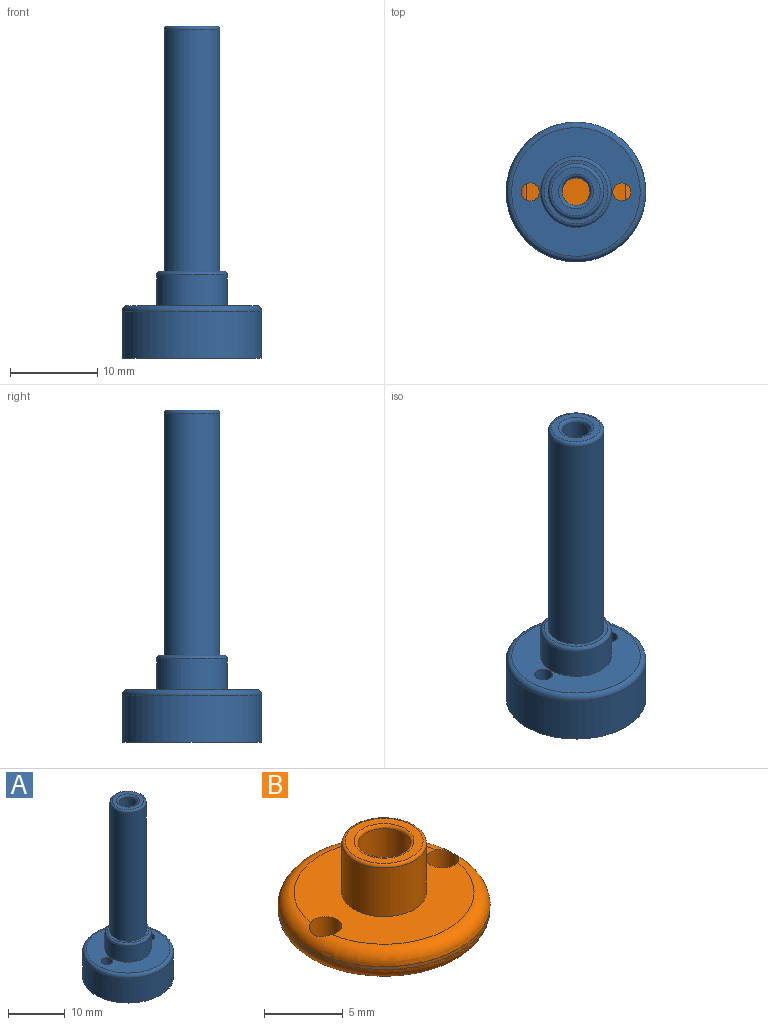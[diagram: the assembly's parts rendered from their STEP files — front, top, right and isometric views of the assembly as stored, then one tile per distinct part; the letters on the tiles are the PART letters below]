
ASSEMBLY  parts=2 mates=1
PART A: 22 faces, bbox 17.3x17.3x37.9 mm
  f0: plane 14.71x14.71mm, normal (0,0,-1), area 140.6mm2, adj f4,f5,f20,f21
  f1: plane 14.71x14.71mm, normal (0,0,1), area 111.6mm2, adj f12,f13,f20,f21
  f2: cylinder r=1.59mm len=29.13mm, axis (0,0,1), area 290.6mm2, adj f3,f19
  f3: plane 5.36x5.36mm, normal (0,0,-1), area 14.6mm2, adj f2,f4
  f4: cylinder r=2.68mm len=5.36mm, axis (0,0,1), area 65.9mm2, adj f0,f3
  f5: cylinder r=7.35mm len=14.71mm, axis (0,0,1), area 146.7mm2, adj f0,f6
  f6: plane 15.02x15.02mm, normal (0,0,-1), area 7.3mm2, adj f5,f7
  f7: torus R=7.51mm, axis (0,0,1), area 29.4mm2, adj f6,f8
  f8: cylinder r=7.1mm len=14.2mm, axis (0,0,1), area 22.3mm2, adj f7,f9
  f9: torus R=7.51mm, axis (0,0,1), area 29.4mm2, adj f8,f10
  f10: plane 15.98x15.98mm, normal (0,0,-1), area 23.3mm2, adj f9,f11
  f11: cylinder r=7.99mm len=15.98mm, axis (0,0,1), area 269mm2, adj f10,f12
  f12: torus R=7.35mm, axis (0,0,1), area 48.6mm2, adj f1,f11
  f13: cylinder r=4.05mm len=8.1mm, axis (0,0,1), area 89.1mm2, adj f1,f14
  f14: torus R=3.64mm, axis (0,0,1), area 15.8mm2, adj f13,f15
  f15: plane 7.28x7.28mm, normal (0,0,1), area 9.7mm2, adj f14,f16
  f16: cylinder r=3.19mm len=27.63mm, axis (0,0,1), area 553.4mm2, adj f15,f17
  f17: torus R=2.78mm, axis (0,0,1), area 12.3mm2, adj f16,f18
  f18: plane 5.55x5.55mm, normal (0,0,1), area 11.7mm2, adj f17,f19
  f19: torus R=2mm, axis (0,0,1), area 7mm2, adj f2,f18
  f20: cylinder r=1.04mm len=2.07mm, axis (0,0,1), area 9.7mm2, adj f0,f1
  f21: cylinder r=1.04mm len=2.07mm, axis (0,0,1), area 9.7mm2, adj f0,f1
PART B: 13 faces, bbox 14.5x14.5x6.2 mm
  f0: plane 11.4x11.24mm, normal (0,0,-1), area 97mm2, adj f1,f11,f12
  f1: torus R=5.7mm, axis (0,0,1), area 62mm2, adj f0,f4,f11,f12
  f2: torus R=5.7mm, axis (0,0,1), area 62mm2, adj f3,f4,f11,f12
  f3: plane 11.4x11.24mm, normal (0,0,1), area 74.5mm2, adj f2,f5,f11,f12
  f4: cylinder r=6.72mm len=13.44mm, axis (0,0,1), area 9.6mm2, adj f1,f2
  f5: cylinder r=2.68mm len=5.36mm, axis (0,0,1), area 63.7mm2, adj f3,f6
  f6: torus R=2.47mm, axis (0,0,1), area 5.3mm2, adj f5,f7
  f7: plane 4.95x4.95mm, normal (0,0,1), area 7.9mm2, adj f6,f8
  f8: torus R=1.9mm, axis (0,0,1), area 4mm2, adj f7,f9
  f9: cylinder r=1.66mm len=3.75mm, axis (0,0,1), area 39.2mm2, adj f8,f10
  f10: plane 3.33x3.33mm, normal (0,0,1), area 8.7mm2, adj f9
  f11: cylinder r=1.04mm len=2.26mm, axis (0,0,1), area 14.3mm2, adj f0,f1,f2,f3
  f12: cylinder r=1.04mm len=2.26mm, axis (0,0,1), area 14.3mm2, adj f0,f1,f2,f3
PLACE A at identity fixed
PLACE B rot(axis=(0,0,-1),110.7deg) t=(0,0,0.9)mm
MATE cylindrical A.f2 <-> B.f1  axis (0,0,1) through (0,0,2.68)mm
